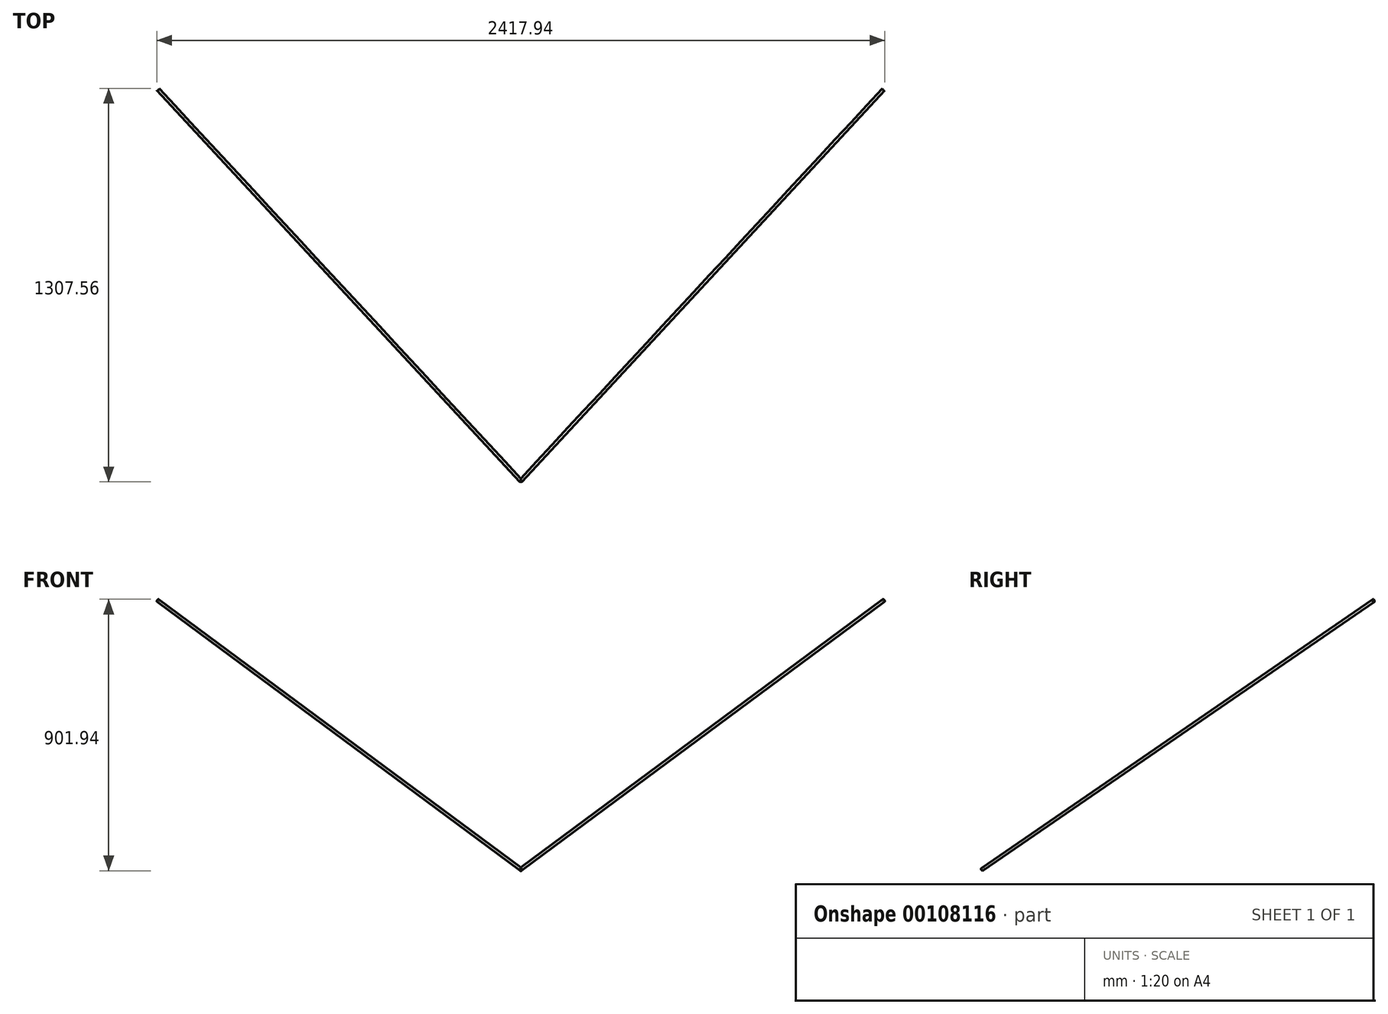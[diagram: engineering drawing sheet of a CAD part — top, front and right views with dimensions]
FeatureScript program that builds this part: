
annotation { "Feature Type Name" : "Feature", "Feature Type Description" : "" }
export const myFeature = defineFeature(function(context is Context, id is Id, definition is map)
    precondition{}
    {
        {
            assignVariable(context, id + "F0", {"name" : "Y1", "anyValue" : 0});
        }
        {
            var Q0;
            Q0=qCreatedBy(makeId("Front.planeOp"),FACE);
            cPlane(context, id + "F1", {"entities" : qUnion([Q0]), "cplaneType" : CPlaneType.OFFSET, "offset" : (getVariable(context, 'Y1')) * mm, "width" : 150 * mm, "height" : 150 * mm});
        }
        {
            var Q0;
            Q0=qCreatedBy(id+"F1.planeOp",FACE);
            var sketch = newSketch(context, id + "F2", { "sketchPlane" : qUnion([Q0])});
            skPoint(sketch, "E0", {"position": v(-1205, 5550) * mm});
            skPoint(sketch, "E1", {"position": v(-1205, 0) * mm});
            skSolve(sketch);
        }
        {
            assignVariable(context, id + "F3", {"name" : "Y2", "anyValue" : 3900 / 2 - 650});
        }
        {
            var Q0;
            Q0=qCreatedBy(makeId("Front.planeOp"),FACE);
            cPlane(context, id + "F4", {"entities" : qUnion([Q0]), "cplaneType" : CPlaneType.OFFSET, "offset" : (getVariable(context, 'Y2')) * mm, "width" : 150 * mm, "height" : 150 * mm});
        }
        {
            var Q0;
            Q0=qCreatedBy(id+"F4.planeOp",FACE);
            var sketch = newSketch(context, id + "F5", { "sketchPlane" : qUnion([Q0])});
            skPoint(sketch, "E2", {"position": v(0, 4657) * mm});
            skSolve(sketch);
        }
        {
            var Q0;
            Q0=sQuery(id+"F2.wireOp",VERTEX,"E0");
            var Q1;
            Q1=sQuery(id+"F2.wireOp",VERTEX,"E1");
            var Q2;
            Q2=sQuery(id+"F5.wireOp",VERTEX,"E2");
            cPlane(context, id + "F6", {"entities" : qUnion([Q0, Q1, Q2]), "cplaneType" : CPlaneType.THREE_POINT, "offset" : 25 * mm, "width" : 150 * mm, "height" : 150 * mm});
        }
        {
            var Q0;
            Q0=qCreatedBy(id+"F6.planeOp",FACE);
            var sketch = newSketch(context, id + "F7", { "sketchPlane" : qUnion([Q0])});
            skPoint(sketch, "E3.0", {"position": v(819.16, 5550) * mm});
            skPoint(sketch, "E4.0", {"position": v(-953.41, 4657) * mm});
            skLineSegment(sketch, "E5", {"start": v(819.16, 5550) * mm, "end": v(-953.41, 4657) * mm});
            skSolve(sketch);
        }
        {
            var Q0;
            Q0=sQuery(id+"F7.wireOp",VERTEX,"E3.0");
            var Q1;
            Q1=sQuery(id+"F7.wireOp",EDGE,"E5");
            cPlane(context, id + "F8", {"entities" : qUnion([Q0, Q1]), "cplaneType" : CPlaneType.LINE_POINT, "offset" : 25 * mm, "width" : 150 * mm, "height" : 150 * mm});
        }
        {
            var Q0;
            Q0=qCreatedBy(id+"F8.planeOp",FACE);
            var sketch = newSketch(context, id + "F9", { "sketchPlane" : qUnion([Q0])});
            skPoint(sketch, "E6.0", {"position": v(950.3, 4574.66) * mm});
            skCircle(sketch, "E7", {"center": v(950.3, 4574.66) * mm, "radius": 5 * mm});
            skSolve(sketch);
        }
        {
            var Q0;
            Q0=makeQuery(id+"F9.imprint","IMPRINT",FACE,{"disambiguationData":[TD([[makeQuery(id+"F9.imprint","IMPRINT",EDGE,{"derivedFrom":sQuery(id+"F9.wireOp",EDGE,"E7")}),1.0]])]});
            var Q1;
            Q1=sQuery(id+"F7.wireOp",EDGE,"E5");
            sweep(context, id + "F10", {"profiles" : qUnion([Q0]), "path" : qUnion([Q1])});
        }
        {
            var Q0;
            Q0=makeQuery(id+"F10.opSweep","SWEPT_BODY",BODY,{"disambiguationData":[OSD([sQuery(id+"F7.wireOp",EDGE,"E5"),sQuery(id+"F9.wireOp",EDGE,"E7")])]});
            var Q1;
            Q1=qCreatedBy(makeId("Right.planeOp"),FACE);
            mirror(context, id + "F11", {"operationType" : NewBodyOperationType.ADD, "entities" : qUnion([Q0]), "mirrorPlane" : qUnion([Q1])});
        }
    });
